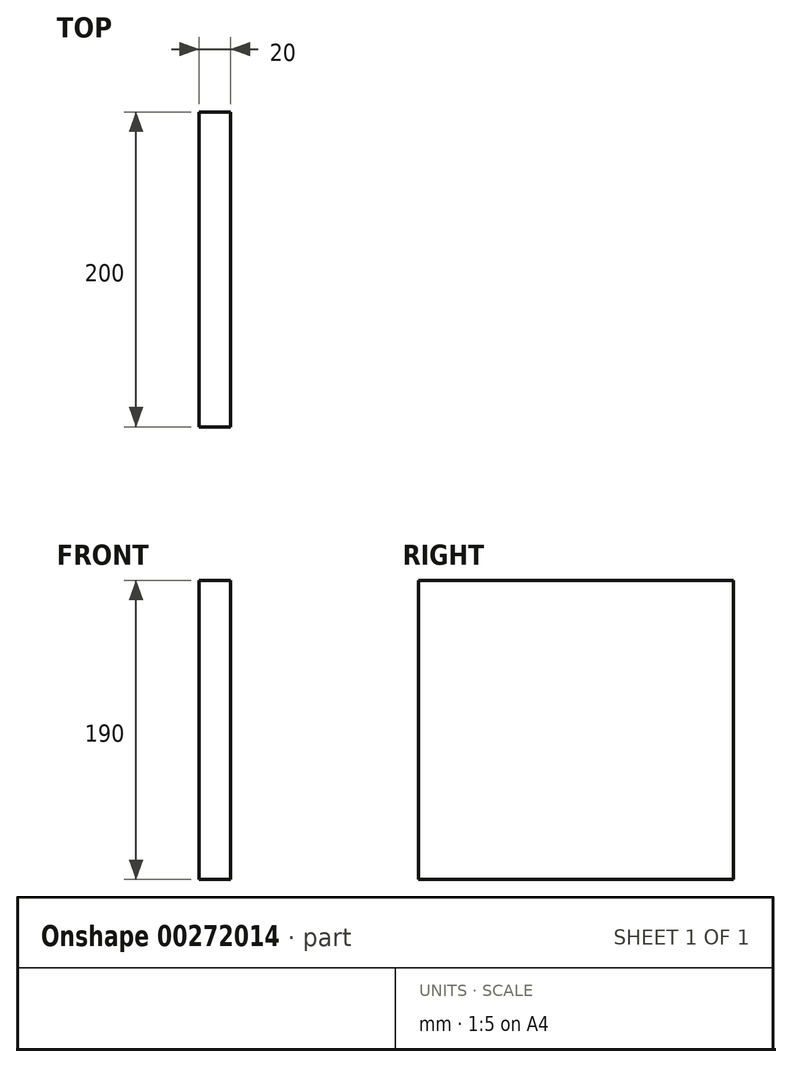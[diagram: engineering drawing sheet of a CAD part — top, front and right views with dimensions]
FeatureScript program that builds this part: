
annotation { "Feature Type Name" : "Feature", "Feature Type Description" : "" }
export const myFeature = defineFeature(function(context is Context, id is Id, definition is map)
    precondition{}
    {
        {
            var Q0;
            Q0=qCreatedBy(makeId("Front.planeOp"),FACE);
            var sketch = newSketch(context, id + "F0", { "sketchPlane" : qUnion([Q0])});
            skLineSegment(sketch, "E0.bottom", {"start": v(0, 0) * mm, "end": v(20, 0) * mm});
            skLineSegment(sketch, "E0.top", {"start": v(0, -190) * mm, "end": v(20, -190) * mm});
            skLineSegment(sketch, "E0.left", {"start": v(0, 0) * mm, "end": v(0, -190) * mm});
            skLineSegment(sketch, "E0.right", {"start": v(20, 0) * mm, "end": v(20, -190) * mm});
            skSolve(sketch);
        }
        {
            var Q0;
            Q0=makeQuery(id+"F0.imprint","IMPRINT",FACE,{"disambiguationData":[TD([[makeQuery(id+"F0.imprint","IMPRINT",EDGE,{"derivedFrom":sQuery(id+"F0.wireOp",EDGE,"E0.bottom")}),-1.0]])]});
            extrude(context, id + "F1", {"entities" : qUnion([Q0]), "oppositeDirection" : true, "depth" : 200 * mm});
        }
    });
